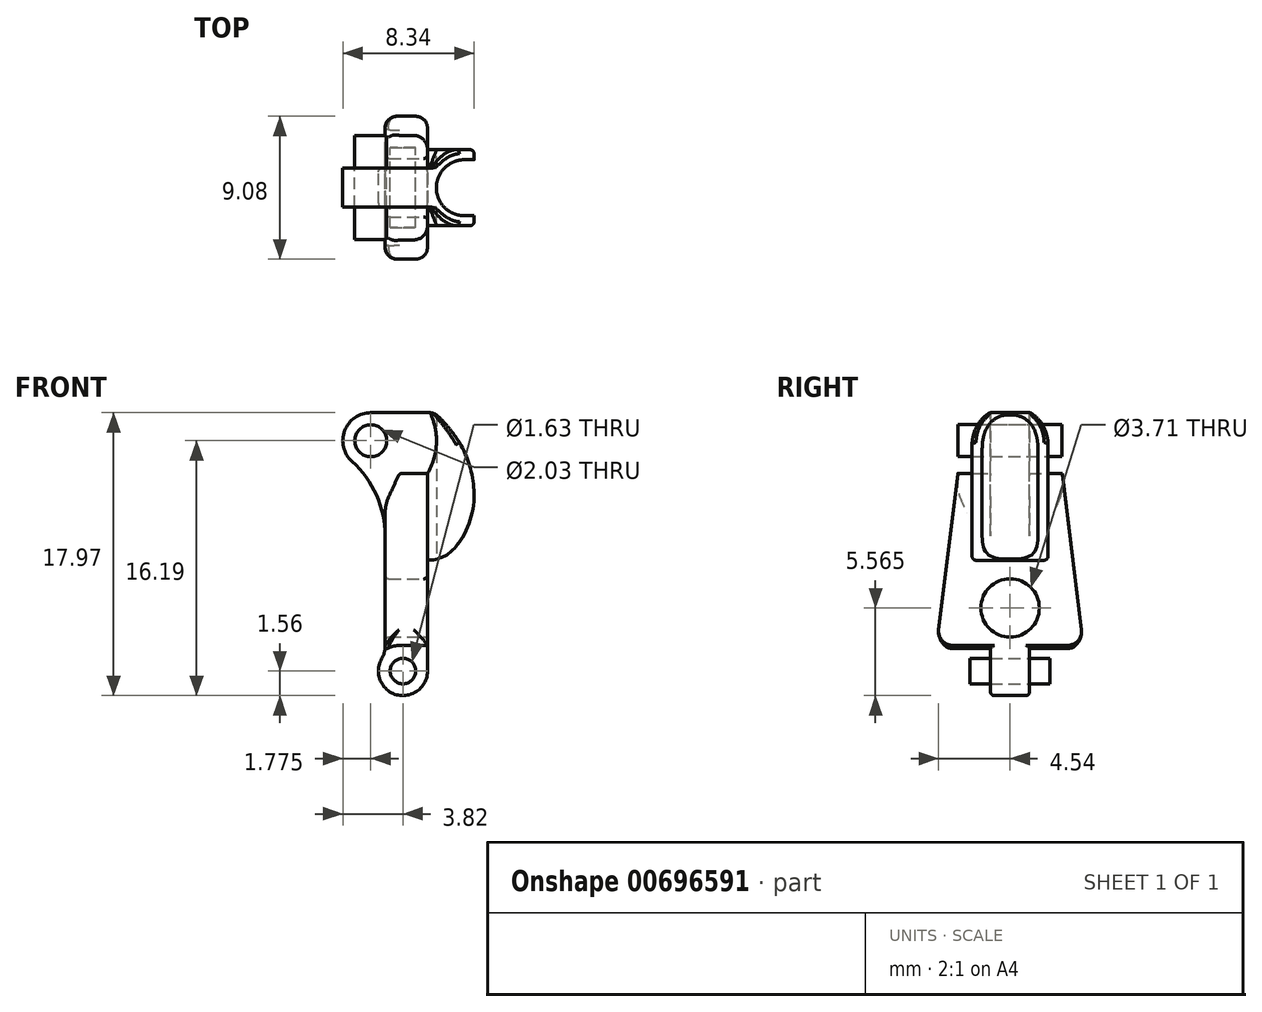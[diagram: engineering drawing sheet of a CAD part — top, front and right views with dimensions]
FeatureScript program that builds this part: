
annotation { "Feature Type Name" : "Feature", "Feature Type Description" : "" }
export const myFeature = defineFeature(function(context is Context, id is Id, definition is map)
    precondition{}
    {
        {
            var Q0;
            Q0=qCreatedBy(makeId("Front.planeOp"),FACE);
            var sketch = newSketch(context, id + "F0", { "sketchPlane" : qUnion([Q0])});
            skCircle(sketch, "E0", {"center": v(0, 0) * mm, "radius": 0.81 * mm});
            skArc(sketch, "E1", {"start": v(-1.35, 0.8) * mm, "mid": v(-0.41, -1.5) * mm, "end": v(1.56, 0) * mm});
            skArc(sketch, "E2", {"start": v(-1.13, 8.59) * mm, "mid": v(-1.68, 11.17) * mm, "end": v(-3.23, 13.3) * mm});
            skArc(sketch, "E3", {"start": v(-3.23, 13.3) * mm, "mid": v(-3.7, 15.27) * mm, "end": v(-2.04, 16.4) * mm});
            skPoint(sketch, "E3.endSnap0", {"position": v(-2.04, 10.94) * mm});
            skLineSegment(sketch, "E4", {"start": v(1.56, 12.55) * mm, "end": v(1.56, 0) * mm});
            skCircle(sketch, "E5", {"center": v(-2.04, 14.63) * mm, "radius": 1.02 * mm});
            skArc(sketch, "E6", {"start": v(1.56, 12.55) * mm, "mid": v(2.13, 14.46) * mm, "end": v(1.72, 16.4) * mm});
            skLineSegment(sketch, "E7", {"start": v(-2.04, 16.4) * mm, "end": v(1.72, 16.4) * mm});
            skArc(sketch, "E8", {"start": v(-1.35, 0.8) * mm, "mid": v(-1.19, 1.17) * mm, "end": v(-1.13, 1.58) * mm});
            skLineSegment(sketch, "E9", {"start": v(-1.13, 1.58) * mm, "end": v(-1.13, 8.59) * mm});
            skSolve(sketch);
        }
        {
            var Q0;
            Q0=qSketchRegion(id+"F0",true);
            extrude(context, id + "F1", {"entities" : qUnion([Q0]), "depth" : 2.5 * mm, "offsetDistance" : 25.4 * mm, "symmetric" : true});
        }
        {
            var Q0;
            Q0=qCreatedBy(makeId("Front.planeOp"),FACE);
            var sketch = newSketch(context, id + "F2", { "sketchPlane" : qUnion([Q0])});
            skLineSegment(sketch, "E10", {"start": v(-0.34, 7.04) * mm, "end": v(4.84, 7.04) * mm, "construction": true});
            skPoint(sketch, "E11", {"position": v(-2.04, 14.63) * mm});
            skArc(sketch, "E12", {"start": v(3.14, 15.16) * mm, "mid": v(2.6, 15.81) * mm, "end": v(2, 16.4) * mm});
            skLineSegment(sketch, "E13", {"start": v(1.56, 7.04) * mm, "end": v(1.56, 7.04) * mm});
            skArc(sketch, "E14.0", {"start": v(1.56, 12.55) * mm, "mid": v(2.13, 14.46) * mm, "end": v(1.72, 16.4) * mm});
            skLineSegment(sketch, "E15.0", {"start": v(1.56, 12.55) * mm, "end": v(1.56, 0) * mm});
            skLineSegment(sketch, "E16", {"start": v(1.72, 16.4) * mm, "end": v(2, 16.4) * mm});
            skArc(sketch, "E17", {"start": v(3.14, 15.16) * mm, "mid": v(4.1, 13.42) * mm, "end": v(4.5, 11.48) * mm});
            skArc(sketch, "E18", {"start": v(4.5, 11.48) * mm, "mid": v(4.27, 9.58) * mm, "end": v(3.37, 7.9) * mm});
            skArc(sketch, "E19", {"start": v(3.37, 7.9) * mm, "mid": v(2.56, 7.26) * mm, "end": v(1.56, 7.04) * mm});
            skSolve(sketch);
        }
        {
            var Q0;
            Q0=qSketchRegion(id+"F2",true);
            extrude(context, id + "F3", {"entities" : qUnion([Q0]), "operationType" : NewBodyOperationType.ADD, "depth" : 4.83 * mm, "offsetDistance" : 25.4 * mm, "symmetric" : true});
        }
        {
            var Q0;
            Q0=qCreatedBy(makeId("Front.planeOp"),FACE);
            var sketch = newSketch(context, id + "F4", { "sketchPlane" : qUnion([Q0])});
            skLineSegment(sketch, "E20", {"start": v(1.56, 1.63) * mm, "end": v(-0.2, 1.63) * mm});
            skLineSegment(sketch, "E21", {"start": v(1.56, 1.63) * mm, "end": v(1.56, 12.55) * mm});
            skLineSegment(sketch, "E22", {"start": v(-0.22, 12.55) * mm, "end": v(-0.22, 9.35) * mm, "construction": true});
            skLineSegment(sketch, "E23", {"start": v(-0.22, 12.55) * mm, "end": v(1.56, 12.55) * mm});
            skArc(sketch, "E24", {"start": v(-0.98, 8.59) * mm, "mid": v(-0.44, 8.81) * mm, "end": v(-0.22, 9.35) * mm, "construction": true});
            skLineSegment(sketch, "E25", {"start": v(-0.98, 8.59) * mm, "end": v(-1.13, 8.59) * mm, "construction": true});
            skPoint(sketch, "E26.orphan", {"position": v(-3.23, 13.3) * mm});
            skLineSegment(sketch, "E27.0", {"start": v(-1.13, 1.58) * mm, "end": v(-1.13, 8.59) * mm});
            skArc(sketch, "E28.0", {"start": v(-1.35, 0.8) * mm, "mid": v(-1.27, 0.93) * mm, "end": v(-1.21, 1.08) * mm});
            skPoint(sketch, "E29.orphan", {"position": v(-1.35, 0.8) * mm});
            skPoint(sketch, "E30.visualSharp", {"position": v(-1.21, 1.08) * mm});
            skArc(sketch, "E30.filletArc", {"start": v(-1.13, 1.58) * mm, "mid": v(-1.06, 1.46) * mm, "end": v(-0.92, 1.46) * mm});
            skPoint(sketch, "E31.orphan", {"position": v(-1.13, 1.58) * mm});
            skArc(sketch, "E32", {"start": v(-0.2, 1.63) * mm, "mid": v(-0.57, 1.58) * mm, "end": v(-0.92, 1.46) * mm});
            skCircle(sketch, "E33", {"center": v(0, 0) * mm, "radius": 1.63 * mm, "construction": true});
            skLineSegment(sketch, "E34", {"start": v(-1.13, 8.59) * mm, "end": v(-0.22, 9.35) * mm, "construction": true});
            skLineSegment(sketch, "E35", {"start": v(-0.22, 12.55) * mm, "end": v(-0.9, 11.1) * mm});
            skLineSegment(sketch, "E36", {"start": v(-1.13, 10.03) * mm, "end": v(-1.13, 8.59) * mm});
            skPoint(sketch, "E37.0.visualSharp", {"position": v(-1.13, 10.6) * mm});
            skArc(sketch, "E37.0.filletArc", {"start": v(-0.9, 11.1) * mm, "mid": v(-1.07, 10.58) * mm, "end": v(-1.13, 10.03) * mm});
            skSolve(sketch);
        }
        {
            var Q0;
            Q0=qSketchRegion(id+"F4",true);
            extrude(context, id + "F5", {"entities" : qUnion([Q0]), "operationType" : NewBodyOperationType.ADD, "depth" : 16.26 * mm, "offsetDistance" : 25.4 * mm, "symmetric" : true});
        }
        {
            var Q0;
            Q0=qCreatedBy(makeId("Right.planeOp"),FACE);
            var sketch = newSketch(context, id + "F6", { "sketchPlane" : qUnion([Q0])});
            skLineSegment(sketch, "E38", {"start": v(-4.86, 0) * mm, "end": v(-3.31, 12.55) * mm});
            skLineSegment(sketch, "E39", {"start": v(-3.31, 12.55) * mm, "end": v(-8.13, 12.55) * mm});
            skLineSegment(sketch, "E40", {"start": v(-8.13, 12.55) * mm, "end": v(-8.13, 0) * mm});
            skLineSegment(sketch, "E41", {"start": v(-8.13, 0) * mm, "end": v(-4.86, 0) * mm});
            skLineSegment(sketch, "E42", {"start": v(0, 0) * mm, "end": v(0, 14.48) * mm, "construction": true});
            skLineSegment(sketch, "E43.MirrorCS", {"start": v(4.86, 0) * mm, "end": v(3.31, 12.55) * mm});
            skLineSegment(sketch, "E44.MirrorCS", {"start": v(3.31, 12.55) * mm, "end": v(8.13, 12.55) * mm});
            skLineSegment(sketch, "E45.MirrorCS", {"start": v(8.13, 0) * mm, "end": v(4.86, 0) * mm});
            skLineSegment(sketch, "E46.MirrorCS", {"start": v(8.13, 12.55) * mm, "end": v(8.13, 0) * mm});
            skSolve(sketch);
        }
        {
            var Q0;
            Q0=qSketchRegion(id+"F6",true);
            extrude(context, id + "F7", {"entities" : qUnion([Q0]), "operationType" : NewBodyOperationType.REMOVE, "endBound" : BoundingType.THROUGH_ALL, "depth" : 25.4 * mm, "offsetDistance" : 25.4 * mm, "hasSecondDirection" : true, "secondDirectionBound" : BoundingType.THROUGH_ALL, "secondDirectionOppositeDirection" : true, "secondDirectionDepth" : 25.4 * mm});
        }
        {
            var Q0;
            Q0=qCreatedBy(makeId("Right.planeOp"),FACE);
            var sketch = newSketch(context, id + "F8", { "sketchPlane" : qUnion([Q0])});
            skCircle(sketch, "E47", {"center": v(0, 4) * mm, "radius": 1.85 * mm});
            skSolve(sketch);
        }
        {
            var Q0;
            Q0=qSketchRegion(id+"F8",true);
            extrude(context, id + "F9", {"entities" : qUnion([Q0]), "operationType" : NewBodyOperationType.REMOVE, "endBound" : BoundingType.THROUGH_ALL, "oppositeDirection" : true, "depth" : 25.4 * mm, "offsetDistance" : 25.4 * mm, "hasSecondDirection" : true, "secondDirectionBound" : BoundingType.THROUGH_ALL, "secondDirectionOppositeDirection" : false, "secondDirectionDepth" : 25.4 * mm});
        }
        {
            var Q0;
            Q0=makeQuery(id+"F3.opExtrude","SWEPT_EDGE",EDGE,{"disambiguationData":[OSD([sQuery(id+"F2.wireOp",EDGE,"E12"),sQuery(id+"F2.wireOp",EDGE,"E16")])]});
            fillet(context, id + "F10", {"entities" : qUnion([Q0]), "radius" : 0.8 * mm, "tangentPropagation" : true, "allowEdgeOverflow" : false});
        }
        {
            var Q0;
            Q0=qCreatedBy(makeId("Top.planeOp"),FACE);
            var sketch = newSketch(context, id + "F11", { "sketchPlane" : qUnion([Q0])});
            skArc(sketch, "E48", {"start": v(3.9, 1.78) * mm, "mid": v(2.12, 0) * mm, "end": v(3.9, -1.78) * mm});
            skLineSegment(sketch, "E49.bottom", {"start": v(3.9, 1.78) * mm, "end": v(8.98, 1.78) * mm});
            skLineSegment(sketch, "E49.top", {"start": v(3.9, -1.78) * mm, "end": v(8.98, -1.78) * mm});
            skLineSegment(sketch, "E49.left", {"start": v(3.9, 1.78) * mm, "end": v(3.9, -1.78) * mm});
            skLineSegment(sketch, "E49.right", {"start": v(8.98, 1.78) * mm, "end": v(8.98, -1.78) * mm});
            skSolve(sketch);
        }
        {
            var Q0;
            Q0=qSketchRegion(id+"F11",true);
            extrude(context, id + "F12", {"entities" : qUnion([Q0]), "operationType" : NewBodyOperationType.REMOVE, "endBound" : BoundingType.THROUGH_ALL, "depth" : 25.4 * mm, "offsetDistance" : 25.4 * mm});
        }
        {
            var Q0;
            Q0=qCreatedBy(makeId("Right.planeOp"),FACE);
            var sketch = newSketch(context, id + "F13", { "sketchPlane" : qUnion([Q0])});
            skArc(sketch, "E50", {"start": v(2.41, 14.38) * mm, "mid": v(0, 16.79) * mm, "end": v(-2.41, 14.38) * mm});
            skLineSegment(sketch, "E51", {"start": v(-2.41, 14.38) * mm, "end": v(-2.41, 18.19) * mm});
            skLineSegment(sketch, "E52", {"start": v(-2.41, 18.19) * mm, "end": v(2.41, 18.19) * mm});
            skLineSegment(sketch, "E53", {"start": v(2.41, 18.19) * mm, "end": v(2.41, 14.38) * mm});
            skSolve(sketch);
        }
        {
            var Q0;
            Q0=qSketchRegion(id+"F13",true);
            extrude(context, id + "F14", {"entities" : qUnion([Q0]), "operationType" : NewBodyOperationType.REMOVE, "endBound" : BoundingType.THROUGH_ALL, "depth" : 25.4 * mm, "offsetDistance" : 25.4 * mm});
        }
        {
            var Q0;
            Q0=makeQuery(id+"F0.imprint","IMPRINT",FACE,{"disambiguationData":[TD([[makeQuery(id+"F0.imprint","IMPRINT",EDGE,{"derivedFrom":sQuery(id+"F0.wireOp",EDGE,"E0")}),1.0]])]});
            extrude(context, id + "F15", {"entities" : qUnion([Q0]), "flatOperationType" : FlatOperationType.REMOVE, "depth" : 5.08 * mm, "offsetDistance" : 25.4 * mm, "domain" : OperationDomain.MODEL, "symmetric" : true});
        }
        {
            var Q0;
            Q0=makeQuery(id+"F0.imprint","IMPRINT",FACE,{"disambiguationData":[TD([[makeQuery(id+"F0.imprint","IMPRINT",EDGE,{"derivedFrom":sQuery(id+"F0.wireOp",EDGE,"E5")}),1.0]])]});
            extrude(context, id + "F16", {"entities" : qUnion([Q0]), "flatOperationType" : FlatOperationType.REMOVE, "depth" : 6.6 * mm, "offsetDistance" : 25.4 * mm, "domain" : OperationDomain.MODEL, "symmetric" : true});
        }
        {
            var Q0;
            Q0=qCreatedBy(makeId("Top.planeOp"),FACE);
            cPlane(context, id + "F17", {"entities" : qUnion([Q0]), "cplaneType" : CPlaneType.OFFSET, "offset" : 6.1 * mm, "width" : 152.4 * mm, "height" : 152.4 * mm});
        }
        {
            var Q0;
            Q0=qCreatedBy(makeId("Front.planeOp"),FACE);
            var sketch = newSketch(context, id + "F18", { "sketchPlane" : qUnion([Q0])});
            skLineSegment(sketch, "E54", {"start": v(-7.6, 3.7) * mm, "end": v(1.35, 6.1) * mm, "construction": true});
            skSolve(sketch);
        }
        {
            var Q0;
            {var subQ0=sQuery(id+"F4.wireOp",EDGE,"E23");var subQ1=sQuery(id+"F4.wireOp",EDGE,"E22");Q0=makeQuery(id+"F5.boolean.opBoolean","SPLIT",EDGE,{"disambiguationData":[TD([makeQuery(id+"F1.opExtrude","CAP_FACE",FACE,{"disambiguationData":[OSD([sQuery(id+"F0.wireOp",EDGE,"E0"),sQuery(id+"F0.wireOp",EDGE,"E1"),sQuery(id+"F0.wireOp",EDGE,"mG3sy2jd-m9rH-R9pf-XSXa-JpG3MHaMja1S"),sQuery(id+"F0.wireOp",EDGE,"E2"),sQuery(id+"F0.wireOp",EDGE,"E3"),sQuery(id+"F0.wireOp",EDGE,"E4"),sQuery(id+"F0.wireOp",EDGE,"E5"),sQuery(id+"F0.wireOp",EDGE,"E6"),sQuery(id+"F0.wireOp",EDGE,"E7")])],"isStart":true})])],"derivedFrom":makeQuery(id+"F5.opExtrude","SWEPT_EDGE",EDGE,{"disambiguationData":[OSD([subQ1,subQ0])]})});}
            var Q1;
            {var subQ0=sQuery(id+"F4.wireOp",EDGE,"E23");var subQ1=sQuery(id+"F4.wireOp",EDGE,"E22");Q1=makeQuery(id+"F5.boolean.opBoolean","SPLIT",EDGE,{"disambiguationData":[TD([makeQuery(id+"F1.opExtrude","CAP_FACE",FACE,{"disambiguationData":[OSD([sQuery(id+"F0.wireOp",EDGE,"E0"),sQuery(id+"F0.wireOp",EDGE,"E1"),sQuery(id+"F0.wireOp",EDGE,"mG3sy2jd-m9rH-R9pf-XSXa-JpG3MHaMja1S"),sQuery(id+"F0.wireOp",EDGE,"E2"),sQuery(id+"F0.wireOp",EDGE,"E3"),sQuery(id+"F0.wireOp",EDGE,"E4"),sQuery(id+"F0.wireOp",EDGE,"E5"),sQuery(id+"F0.wireOp",EDGE,"E6"),sQuery(id+"F0.wireOp",EDGE,"E7")])],"isStart":false})])],"derivedFrom":makeQuery(id+"F5.opExtrude","SWEPT_EDGE",EDGE,{"disambiguationData":[OSD([subQ1,subQ0])]})});}
            fillet(context, id + "F19", {"entities" : qUnion([Q0, Q1]), "radius" : 0.25 * mm, "tangentPropagation" : true, "allowEdgeOverflow" : false});
        }
        {
            var Q0;
            Q0=makeQuery(id+"F12.boolean.opBoolean","INTERSECT",EDGE,{"derivedFrom":[makeQuery(id+"F3.opExtrude","SWEPT_FACE",FACE,{"disambiguationData":[OSD([sQuery(id+"F2.wireOp",EDGE,"29de3570-782e-4213-bd4b-269aa0eefef4")])]}),makeQuery(id+"F12.opExtrude","SWEPT_FACE",FACE,{"disambiguationData":[OSD([sQuery(id+"F11.wireOp",EDGE,"E49.bottom")])]})]});
            var Q1;
            Q1=makeQuery(id+"F3.opExtrude","CAP_EDGE",EDGE,{"disambiguationData":[OSD([sQuery(id+"F2.wireOp",EDGE,"29de3570-782e-4213-bd4b-269aa0eefef4")])],"isStart":true});
            var Q2;
            Q2=makeQuery(id+"F3.opExtrude","CAP_EDGE",EDGE,{"disambiguationData":[OSD([sQuery(id+"F2.wireOp",EDGE,"29de3570-782e-4213-bd4b-269aa0eefef4")])],"isStart":false});
            var Q3;
            Q3=makeQuery(id+"F3.opExtrude","CAP_EDGE",EDGE,{"disambiguationData":[OSD([sQuery(id+"F2.wireOp",EDGE,"E18")])],"isStart":true});
            var Q4;
            Q4=makeQuery(id+"F3.opExtrude","CAP_EDGE",EDGE,{"disambiguationData":[OSD([sQuery(id+"F2.wireOp",EDGE,"E17")])],"isStart":false});
            fillet(context, id + "F20", {"entities" : qUnion([Q0, Q1, Q2, Q3, Q4]), "radius" : 0.25 * mm, "tangentPropagation" : true, "allowEdgeOverflow" : false});
        }
        {
            var Q0;
            Q0=makeQuery(id+"F7.boolean.opBoolean","INTERSECT",EDGE,{"derivedFrom":[makeQuery(id+"F5.boolean.opBoolean","MERGE",FACE,{"derivedFrom":[makeQuery(id+"F1.opExtrude","SWEPT_FACE",FACE,{"disambiguationData":[OSD([sQuery(id+"F0.wireOp",EDGE,"E9")])]}),makeQuery(id+"F5.opExtrude","SWEPT_FACE",FACE,{"disambiguationData":[OSD([sQuery(id+"F4.wireOp",EDGE,"E27.0")])]})]}),makeQuery(id+"F7.opExtrude","SWEPT_FACE",FACE,{"disambiguationData":[OSD([sQuery(id+"F6.wireOp",EDGE,"E43.MirrorCS")])]})]});
            var Q1;
            Q1=makeQuery(id+"F7.boolean.opBoolean","INTERSECT",EDGE,{"derivedFrom":[makeQuery(id+"F5.boolean.opBoolean","MERGE",FACE,{"derivedFrom":[makeQuery(id+"F1.opExtrude","SWEPT_FACE",FACE,{"disambiguationData":[OSD([sQuery(id+"F0.wireOp",EDGE,"E4")])]}),makeQuery(id+"F5.opExtrude","SWEPT_FACE",FACE,{"disambiguationData":[OSD([sQuery(id+"F4.wireOp",EDGE,"E21")])]})]}),makeQuery(id+"F7.opExtrude","SWEPT_FACE",FACE,{"disambiguationData":[OSD([sQuery(id+"F6.wireOp",EDGE,"E43.MirrorCS")])]})]});
            var Q2;
            {var subQ0=sQuery(id+"F4.wireOp",EDGE,"43d850ac-2440-44df-8808-e2c5affae032");var subQ1=sQuery(id+"F4.wireOp",EDGE,"E21");var subQ2=sQuery(id+"F4.wireOp",EDGE,"E20");Q2=makeQuery(id+"F7.boolean.opBoolean","INTERSECT",EDGE,{"derivedFrom":[makeQuery(id+"F5.boolean.opBoolean","SPLIT",FACE,{"disambiguationData":[TD([makeQuery(id+"F5.opExtrude","CAP_FACE",FACE,{"disambiguationData":[OSD([subQ2,subQ0,subQ1,sQuery(id+"F4.wireOp",EDGE,"E22"),sQuery(id+"F4.wireOp",EDGE,"E23"),sQuery(id+"F4.wireOp",EDGE,"E24"),sQuery(id+"F4.wireOp",EDGE,"E25"),sQuery(id+"F4.wireOp",EDGE,"E27.0"),sQuery(id+"F4.wireOp",EDGE,"E30.filletArc")])],"isStart":true})])],"derivedFrom":makeQuery(id+"F5.opExtrude","SWEPT_FACE",FACE,{"disambiguationData":[OSD([subQ2])]})}),makeQuery(id+"F7.opExtrude","SWEPT_FACE",FACE,{"disambiguationData":[OSD([sQuery(id+"F6.wireOp",EDGE,"E43.MirrorCS")])]})]});}
            var Q3;
            {var subQ0=sQuery(id+"F4.wireOp",EDGE,"E20");var subQ1=sQuery(id+"F4.wireOp",EDGE,"E30.filletArc");var subQ2=sQuery(id+"F4.wireOp",EDGE,"43d850ac-2440-44df-8808-e2c5affae032");Q3=makeQuery(id+"F7.boolean.opBoolean","INTERSECT",EDGE,{"derivedFrom":[makeQuery(id+"F5.boolean.opBoolean","SPLIT",FACE,{"disambiguationData":[TD([makeQuery(id+"F5.opExtrude","CAP_FACE",FACE,{"disambiguationData":[OSD([subQ0,subQ2,sQuery(id+"F4.wireOp",EDGE,"E21"),sQuery(id+"F4.wireOp",EDGE,"E22"),sQuery(id+"F4.wireOp",EDGE,"E23"),sQuery(id+"F4.wireOp",EDGE,"E24"),sQuery(id+"F4.wireOp",EDGE,"E25"),sQuery(id+"F4.wireOp",EDGE,"E27.0"),subQ1])],"isStart":true})])],"derivedFrom":makeQuery(id+"F5.opExtrude","SWEPT_FACE",FACE,{"disambiguationData":[OSD([subQ2])]})}),makeQuery(id+"F7.opExtrude","SWEPT_FACE",FACE,{"disambiguationData":[OSD([sQuery(id+"F6.wireOp",EDGE,"E43.MirrorCS")])]})]});}
            var Q4;
            {var subQ0=sQuery(id+"F4.wireOp",EDGE,"E27.0");var subQ1=sQuery(id+"F4.wireOp",EDGE,"E25");var subQ2=sQuery(id+"F4.wireOp",EDGE,"E24");Q4=makeQuery(id+"F7.boolean.opBoolean","INTERSECT",EDGE,{"derivedFrom":[makeQuery(id+"F5.boolean.opBoolean","SPLIT",FACE,{"disambiguationData":[TD([makeQuery(id+"F5.opExtrude","CAP_FACE",FACE,{"disambiguationData":[OSD([sQuery(id+"F4.wireOp",EDGE,"E20"),sQuery(id+"F4.wireOp",EDGE,"43d850ac-2440-44df-8808-e2c5affae032"),sQuery(id+"F4.wireOp",EDGE,"E21"),sQuery(id+"F4.wireOp",EDGE,"E22"),sQuery(id+"F4.wireOp",EDGE,"E23"),subQ2,subQ1,subQ0,sQuery(id+"F4.wireOp",EDGE,"E30.filletArc")])],"isStart":true})])],"derivedFrom":makeQuery(id+"F5.opExtrude","SWEPT_FACE",FACE,{"disambiguationData":[OSD([subQ1])]})}),makeQuery(id+"F7.opExtrude","SWEPT_FACE",FACE,{"disambiguationData":[OSD([sQuery(id+"F6.wireOp",EDGE,"E43.MirrorCS")])]})]});}
            var Q5;
            {var subQ0=sQuery(id+"F4.wireOp",EDGE,"43d850ac-2440-44df-8808-e2c5affae032");var subQ1=sQuery(id+"F4.wireOp",EDGE,"E30.filletArc");var subQ2=sQuery(id+"F4.wireOp",EDGE,"E27.0");Q5=makeQuery(id+"F7.boolean.opBoolean","INTERSECT",EDGE,{"derivedFrom":[makeQuery(id+"F5.boolean.opBoolean","SPLIT",FACE,{"disambiguationData":[TD([makeQuery(id+"F5.opExtrude","CAP_FACE",FACE,{"disambiguationData":[OSD([sQuery(id+"F4.wireOp",EDGE,"E20"),subQ0,sQuery(id+"F4.wireOp",EDGE,"E21"),sQuery(id+"F4.wireOp",EDGE,"E22"),sQuery(id+"F4.wireOp",EDGE,"E23"),sQuery(id+"F4.wireOp",EDGE,"E24"),sQuery(id+"F4.wireOp",EDGE,"E25"),subQ2,subQ1])],"isStart":true})])],"derivedFrom":makeQuery(id+"F5.opExtrude","SWEPT_FACE",FACE,{"disambiguationData":[OSD([subQ1])]})}),makeQuery(id+"F7.opExtrude","SWEPT_FACE",FACE,{"disambiguationData":[OSD([sQuery(id+"F6.wireOp",EDGE,"E43.MirrorCS")])]})]});}
            var Q6;
            {var subQ0=sQuery(id+"F4.wireOp",EDGE,"E24");var subQ1=sQuery(id+"F4.wireOp",EDGE,"E23");var subQ2=sQuery(id+"F4.wireOp",EDGE,"E22");Q6=makeQuery(id+"F7.boolean.opBoolean","INTERSECT",EDGE,{"derivedFrom":[makeQuery(id+"F5.boolean.opBoolean","SPLIT",FACE,{"disambiguationData":[TD([makeQuery(id+"F5.opExtrude","CAP_FACE",FACE,{"disambiguationData":[OSD([sQuery(id+"F4.wireOp",EDGE,"E20"),sQuery(id+"F4.wireOp",EDGE,"43d850ac-2440-44df-8808-e2c5affae032"),sQuery(id+"F4.wireOp",EDGE,"E21"),subQ2,subQ1,subQ0,sQuery(id+"F4.wireOp",EDGE,"E25"),sQuery(id+"F4.wireOp",EDGE,"E27.0"),sQuery(id+"F4.wireOp",EDGE,"E30.filletArc")])],"isStart":true})])],"derivedFrom":makeQuery(id+"F5.opExtrude","SWEPT_FACE",FACE,{"disambiguationData":[OSD([subQ2])]})}),makeQuery(id+"F7.opExtrude","SWEPT_FACE",FACE,{"disambiguationData":[OSD([sQuery(id+"F6.wireOp",EDGE,"E43.MirrorCS")])]})]});}
            var Q7;
            Q7=makeQuery(id+"F7.boolean.opBoolean","INTERSECT",EDGE,{"derivedFrom":[makeQuery(id+"F5.boolean.opBoolean","MERGE",FACE,{"derivedFrom":[makeQuery(id+"F1.opExtrude","SWEPT_FACE",FACE,{"disambiguationData":[OSD([sQuery(id+"F0.wireOp",EDGE,"E4")])]}),makeQuery(id+"F5.opExtrude","SWEPT_FACE",FACE,{"disambiguationData":[OSD([sQuery(id+"F4.wireOp",EDGE,"E21")])]})]}),makeQuery(id+"F7.opExtrude","SWEPT_FACE",FACE,{"disambiguationData":[OSD([sQuery(id+"F6.wireOp",EDGE,"E38")])]})]});
            var Q8;
            Q8=makeQuery(id+"F7.boolean.opBoolean","INTERSECT",EDGE,{"derivedFrom":[makeQuery(id+"F5.boolean.opBoolean","MERGE",FACE,{"derivedFrom":[makeQuery(id+"F1.opExtrude","SWEPT_FACE",FACE,{"disambiguationData":[OSD([sQuery(id+"F0.wireOp",EDGE,"E9")])]}),makeQuery(id+"F5.opExtrude","SWEPT_FACE",FACE,{"disambiguationData":[OSD([sQuery(id+"F4.wireOp",EDGE,"E27.0")])]})]}),makeQuery(id+"F7.opExtrude","SWEPT_FACE",FACE,{"disambiguationData":[OSD([sQuery(id+"F6.wireOp",EDGE,"E38")])]})]});
            var Q9;
            {var subQ0=sQuery(id+"F4.wireOp",EDGE,"43d850ac-2440-44df-8808-e2c5affae032");var subQ1=sQuery(id+"F4.wireOp",EDGE,"E21");var subQ2=sQuery(id+"F4.wireOp",EDGE,"E20");Q9=makeQuery(id+"F7.boolean.opBoolean","INTERSECT",EDGE,{"derivedFrom":[makeQuery(id+"F5.boolean.opBoolean","SPLIT",FACE,{"disambiguationData":[TD([makeQuery(id+"F5.opExtrude","CAP_FACE",FACE,{"disambiguationData":[OSD([subQ2,subQ0,subQ1,sQuery(id+"F4.wireOp",EDGE,"E22"),sQuery(id+"F4.wireOp",EDGE,"E23"),sQuery(id+"F4.wireOp",EDGE,"E24"),sQuery(id+"F4.wireOp",EDGE,"E25"),sQuery(id+"F4.wireOp",EDGE,"E27.0"),sQuery(id+"F4.wireOp",EDGE,"E30.filletArc")])],"isStart":false})])],"derivedFrom":makeQuery(id+"F5.opExtrude","SWEPT_FACE",FACE,{"disambiguationData":[OSD([subQ2])]})}),makeQuery(id+"F7.opExtrude","SWEPT_FACE",FACE,{"disambiguationData":[OSD([sQuery(id+"F6.wireOp",EDGE,"E38")])]})]});}
            var Q10;
            {var subQ0=sQuery(id+"F4.wireOp",EDGE,"E20");var subQ1=sQuery(id+"F4.wireOp",EDGE,"E30.filletArc");var subQ2=sQuery(id+"F4.wireOp",EDGE,"43d850ac-2440-44df-8808-e2c5affae032");Q10=makeQuery(id+"F7.boolean.opBoolean","INTERSECT",EDGE,{"derivedFrom":[makeQuery(id+"F5.boolean.opBoolean","SPLIT",FACE,{"disambiguationData":[TD([makeQuery(id+"F5.opExtrude","CAP_FACE",FACE,{"disambiguationData":[OSD([subQ0,subQ2,sQuery(id+"F4.wireOp",EDGE,"E21"),sQuery(id+"F4.wireOp",EDGE,"E22"),sQuery(id+"F4.wireOp",EDGE,"E23"),sQuery(id+"F4.wireOp",EDGE,"E24"),sQuery(id+"F4.wireOp",EDGE,"E25"),sQuery(id+"F4.wireOp",EDGE,"E27.0"),subQ1])],"isStart":false})])],"derivedFrom":makeQuery(id+"F5.opExtrude","SWEPT_FACE",FACE,{"disambiguationData":[OSD([subQ2])]})}),makeQuery(id+"F7.opExtrude","SWEPT_FACE",FACE,{"disambiguationData":[OSD([sQuery(id+"F6.wireOp",EDGE,"E38")])]})]});}
            var Q11;
            {var subQ0=sQuery(id+"F4.wireOp",EDGE,"E22");var subQ1=sQuery(id+"F4.wireOp",EDGE,"E25");var subQ2=sQuery(id+"F4.wireOp",EDGE,"E24");Q11=makeQuery(id+"F7.boolean.opBoolean","INTERSECT",EDGE,{"derivedFrom":[makeQuery(id+"F5.boolean.opBoolean","SPLIT",FACE,{"disambiguationData":[TD([makeQuery(id+"F5.opExtrude","CAP_FACE",FACE,{"disambiguationData":[OSD([sQuery(id+"F4.wireOp",EDGE,"E20"),sQuery(id+"F4.wireOp",EDGE,"43d850ac-2440-44df-8808-e2c5affae032"),sQuery(id+"F4.wireOp",EDGE,"E21"),subQ0,sQuery(id+"F4.wireOp",EDGE,"E23"),subQ2,subQ1,sQuery(id+"F4.wireOp",EDGE,"E27.0"),sQuery(id+"F4.wireOp",EDGE,"E30.filletArc")])],"isStart":false})])],"derivedFrom":makeQuery(id+"F5.opExtrude","SWEPT_FACE",FACE,{"disambiguationData":[OSD([subQ2])]})}),makeQuery(id+"F7.opExtrude","SWEPT_FACE",FACE,{"disambiguationData":[OSD([sQuery(id+"F6.wireOp",EDGE,"E38")])]})]});}
            var Q12;
            {var subQ1=sQuery(id+"F4.wireOp",EDGE,"E27.0");var subQ2=sQuery(id+"F4.wireOp",EDGE,"E25");var subQ3=sQuery(id+"F4.wireOp",EDGE,"E24");Q12=makeQuery(id+"F7.boolean.opBoolean","INTERSECT",EDGE,{"derivedFrom":[makeQuery(id+"F5.boolean.opBoolean","SPLIT",FACE,{"disambiguationData":[TD([makeQuery(id+"F5.opExtrude","CAP_FACE",FACE,{"disambiguationData":[OSD([sQuery(id+"F4.wireOp",EDGE,"E20"),sQuery(id+"F4.wireOp",EDGE,"43d850ac-2440-44df-8808-e2c5affae032"),sQuery(id+"F4.wireOp",EDGE,"E21"),sQuery(id+"F4.wireOp",EDGE,"E22"),sQuery(id+"F4.wireOp",EDGE,"E23"),subQ3,subQ2,subQ1,sQuery(id+"F4.wireOp",EDGE,"E30.filletArc")])],"isStart":false})])],"derivedFrom":makeQuery(id+"F5.opExtrude","SWEPT_FACE",FACE,{"disambiguationData":[OSD([subQ2])]})}),makeQuery(id+"F7.opExtrude","SWEPT_FACE",FACE,{"disambiguationData":[OSD([sQuery(id+"F6.wireOp",EDGE,"E38")])]})]});}
            var Q13;
            {var subQ0=sQuery(id+"F4.wireOp",EDGE,"43d850ac-2440-44df-8808-e2c5affae032");var subQ1=sQuery(id+"F4.wireOp",EDGE,"E30.filletArc");var subQ2=sQuery(id+"F4.wireOp",EDGE,"E27.0");Q13=makeQuery(id+"F7.boolean.opBoolean","INTERSECT",EDGE,{"derivedFrom":[makeQuery(id+"F5.boolean.opBoolean","SPLIT",FACE,{"disambiguationData":[TD([makeQuery(id+"F5.opExtrude","CAP_FACE",FACE,{"disambiguationData":[OSD([sQuery(id+"F4.wireOp",EDGE,"E20"),subQ0,sQuery(id+"F4.wireOp",EDGE,"E21"),sQuery(id+"F4.wireOp",EDGE,"E22"),sQuery(id+"F4.wireOp",EDGE,"E23"),sQuery(id+"F4.wireOp",EDGE,"E24"),sQuery(id+"F4.wireOp",EDGE,"E25"),subQ2,subQ1])],"isStart":false})])],"derivedFrom":makeQuery(id+"F5.opExtrude","SWEPT_FACE",FACE,{"disambiguationData":[OSD([subQ1])]})}),makeQuery(id+"F7.opExtrude","SWEPT_FACE",FACE,{"disambiguationData":[OSD([sQuery(id+"F6.wireOp",EDGE,"E38")])]})]});}
            var Q14;
            {var subQ0=sQuery(id+"F4.wireOp",EDGE,"E24");var subQ1=sQuery(id+"F4.wireOp",EDGE,"E23");var subQ2=sQuery(id+"F4.wireOp",EDGE,"E22");Q14=makeQuery(id+"F7.boolean.opBoolean","INTERSECT",EDGE,{"derivedFrom":[makeQuery(id+"F5.boolean.opBoolean","SPLIT",FACE,{"disambiguationData":[TD([makeQuery(id+"F5.opExtrude","CAP_FACE",FACE,{"disambiguationData":[OSD([sQuery(id+"F4.wireOp",EDGE,"E20"),sQuery(id+"F4.wireOp",EDGE,"43d850ac-2440-44df-8808-e2c5affae032"),sQuery(id+"F4.wireOp",EDGE,"E21"),subQ2,subQ1,subQ0,sQuery(id+"F4.wireOp",EDGE,"E25"),sQuery(id+"F4.wireOp",EDGE,"E27.0"),sQuery(id+"F4.wireOp",EDGE,"E30.filletArc")])],"isStart":false})])],"derivedFrom":makeQuery(id+"F5.opExtrude","SWEPT_FACE",FACE,{"disambiguationData":[OSD([subQ2])]})}),makeQuery(id+"F7.opExtrude","SWEPT_FACE",FACE,{"disambiguationData":[OSD([sQuery(id+"F6.wireOp",EDGE,"E38")])]})]});}
            var Q15;
            {var subQ0=sQuery(id+"F4.wireOp",EDGE,"E25");var subQ1=sQuery(id+"F4.wireOp",EDGE,"E24");var subQ2=sQuery(id+"F4.wireOp",EDGE,"E22");Q15=makeQuery(id+"F7.boolean.opBoolean","INTERSECT",EDGE,{"derivedFrom":[makeQuery(id+"F5.boolean.opBoolean","SPLIT",FACE,{"disambiguationData":[TD([makeQuery(id+"F5.opExtrude","CAP_FACE",FACE,{"disambiguationData":[OSD([sQuery(id+"F4.wireOp",EDGE,"E20"),sQuery(id+"F4.wireOp",EDGE,"43d850ac-2440-44df-8808-e2c5affae032"),sQuery(id+"F4.wireOp",EDGE,"E21"),subQ2,sQuery(id+"F4.wireOp",EDGE,"E23"),subQ1,subQ0,sQuery(id+"F4.wireOp",EDGE,"E27.0"),sQuery(id+"F4.wireOp",EDGE,"E30.filletArc")])],"isStart":true})])],"derivedFrom":makeQuery(id+"F5.opExtrude","SWEPT_FACE",FACE,{"disambiguationData":[OSD([subQ1])]})}),makeQuery(id+"F7.opExtrude","SWEPT_FACE",FACE,{"disambiguationData":[OSD([sQuery(id+"F6.wireOp",EDGE,"E43.MirrorCS")])]})]});}
            fillet(context, id + "F21", {"entities" : qUnion([Q0, Q1, Q2, Q3, Q4, Q5, Q6, Q7, Q8, Q9, Q10, Q11, Q12, Q13, Q14, Q15]), "radius" : 0.89 * mm, "defaultsChanged" : true, "vertexSettings" : [], "allowEdgeOverflow" : false});
        }
        {
            var Q0;
            Q0=makeQuery(id+"F9.boolean.opBoolean","INTERSECT",EDGE,{"derivedFrom":[makeQuery(id+"F5.boolean.opBoolean","MERGE",FACE,{"derivedFrom":[makeQuery(id+"F1.opExtrude","SWEPT_FACE",FACE,{"disambiguationData":[OSD([sQuery(id+"F0.wireOp",EDGE,"E9")])]}),makeQuery(id+"F5.opExtrude","SWEPT_FACE",FACE,{"disambiguationData":[OSD([sQuery(id+"F4.wireOp",EDGE,"E27.0")])]})]}),makeQuery(id+"F9.opExtrude","SWEPT_FACE",FACE,{"disambiguationData":[OSD([sQuery(id+"F8.wireOp",EDGE,"E47")])]})]});
            var Q1;
            Q1=makeQuery(id+"F9.boolean.opBoolean","INTERSECT",EDGE,{"derivedFrom":[makeQuery(id+"F5.boolean.opBoolean","MERGE",FACE,{"derivedFrom":[makeQuery(id+"F1.opExtrude","SWEPT_FACE",FACE,{"disambiguationData":[OSD([sQuery(id+"F0.wireOp",EDGE,"E4")])]}),makeQuery(id+"F5.opExtrude","SWEPT_FACE",FACE,{"disambiguationData":[OSD([sQuery(id+"F4.wireOp",EDGE,"E21")])]})]}),makeQuery(id+"F9.opExtrude","SWEPT_FACE",FACE,{"disambiguationData":[OSD([sQuery(id+"F8.wireOp",EDGE,"E47")])]})]});
            fillet(context, id + "F22", {"entities" : qUnion([Q0, Q1]), "radius" : 0.25 * mm, "tangentPropagation" : true, "allowEdgeOverflow" : false});
        }
        {
            var Q0;
            {var subQ0=sQuery(id+"F0.wireOp",EDGE,"E4");Q0=makeQuery(id+"F3.boolean.opBoolean","SPLIT",EDGE,{"disambiguationData":[topologyDisambiguationEdgeConnected([makeQuery(id+"F1.opExtrude","SWEPT_FACE",FACE,{"disambiguationData":[OSD([subQ0])]})])],"derivedFrom":makeQuery(id+"F1.opExtrude","CAP_EDGE",EDGE,{"disambiguationData":[OSD([subQ0])],"isStart":true})});}
            var Q1;
            Q1=makeQuery(id+"F1.opExtrude","CAP_EDGE",EDGE,{"disambiguationData":[OSD([sQuery(id+"F0.wireOp",EDGE,"E1")])],"isStart":false});
            fillet(context, id + "F23", {"entities" : qUnion([Q0, Q1]), "radius" : 0.25 * mm, "tangentPropagation" : true, "allowEdgeOverflow" : false});
        }
    });
